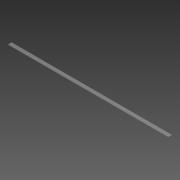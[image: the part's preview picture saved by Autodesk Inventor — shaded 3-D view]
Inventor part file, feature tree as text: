
AUTODESK INVENTOR PART (.ipt)
format: ipt  version: 2013 (Build 170138000, 138)  size: 64,512 bytes
history: native  units: in
note: dims shown in document units (in); Inventor stores cm internally (conversion verified against a paired STEP export)
features: extrude x1, sketch x1
ambient origin geometry x8: Origin, YZ Plane, XZ Plane, XY Plane, X Axis, Y Axis, Z Axis, Center Point
bodies: Solid1 (feature_tree)
feature tree (2):
  extrude  "Extrusion1"  Depth=1.213in
  sketch  "Sketch1"  dims[d0=54.425in d1=1.213in d2=0.2125in d3=0.0in]
